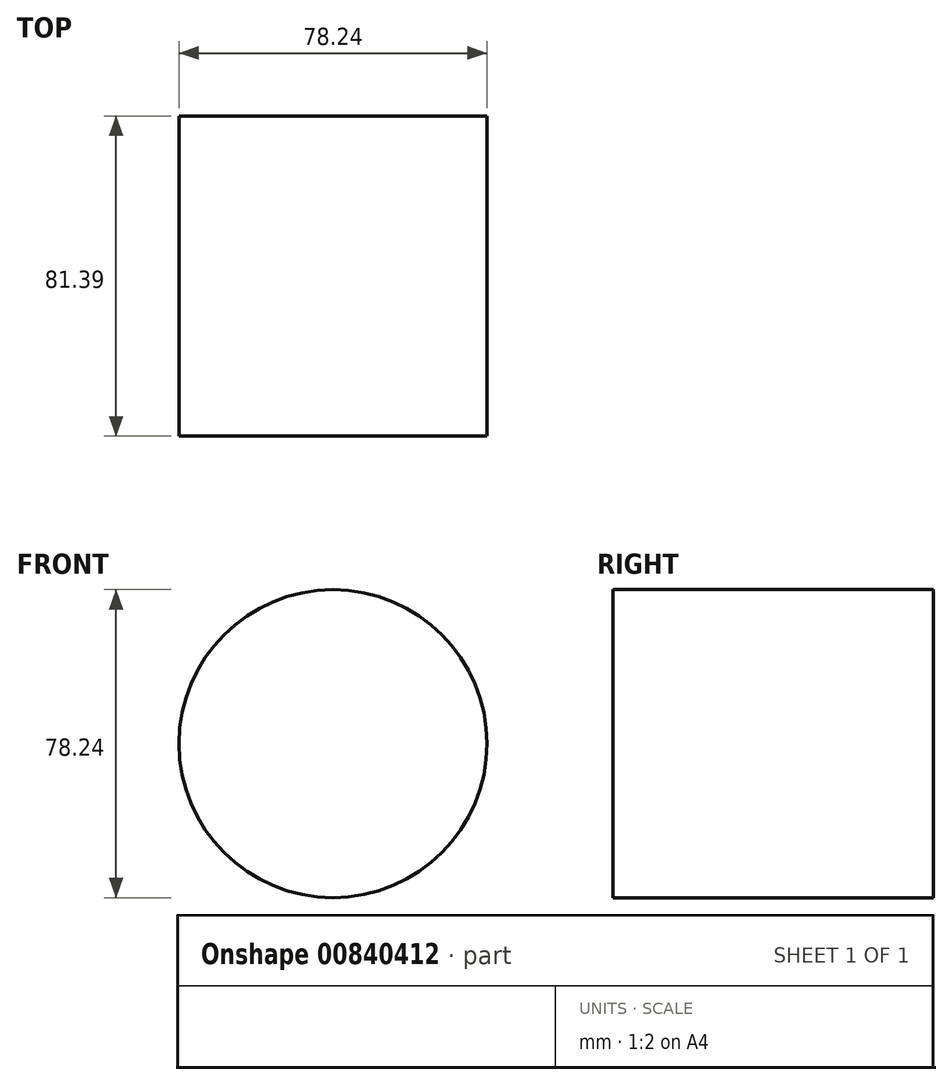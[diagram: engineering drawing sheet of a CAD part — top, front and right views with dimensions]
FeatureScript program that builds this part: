
annotation { "Feature Type Name" : "Feature", "Feature Type Description" : "" }
export const myFeature = defineFeature(function(context is Context, id is Id, definition is map)
    precondition{}
    {
        {
            var Q0;
            Q0=qCreatedBy(makeId("Front.planeOp"),FACE);
            var sketch = newSketch(context, id + "F0", { "sketchPlane" : qUnion([Q0])});
            skCircle(sketch, "E0", {"center": v(0, 11.9) * mm, "radius": 39.12 * mm});
            skSolve(sketch);
        }
        {
            var Q0;
            Q0=makeQuery(id+"F0.imprint","IMPRINT",FACE,{"disambiguationData":[TD([[makeQuery(id+"F0.imprint","IMPRINT",EDGE,{"derivedFrom":sQuery(id+"F0.wireOp",EDGE,"E0")}),1.0]])]});
            extrude(context, id + "F1", {"entities" : qUnion([Q0]), "depth" : 81.4 * mm, "offsetDistance" : 25.4 * mm});
        }
    });
